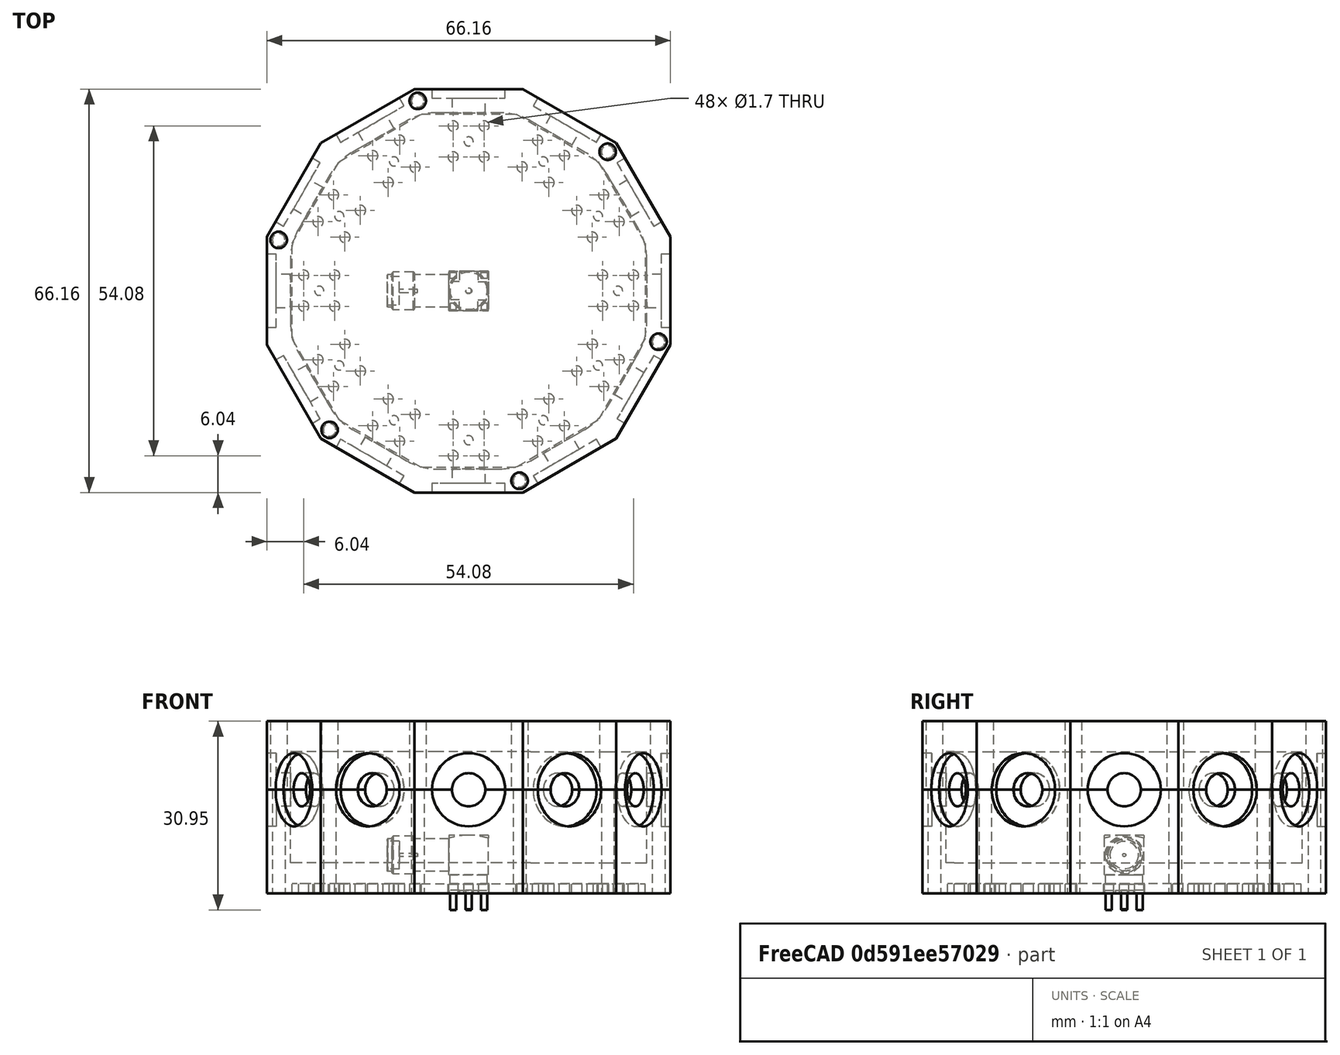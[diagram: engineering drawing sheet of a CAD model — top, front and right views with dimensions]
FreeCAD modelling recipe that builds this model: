
FCSTD DOCUMENT  (FreeCAD 0.19RUnknown)
Label: Case
License: All rights reserved
LicenseURL: http://en.wikipedia.org/wiki/All_rights_reserved
objects: Part::Feature×13, App::Part×13, Sketcher::SketchObject×6, TechDraw::DrawViewPart×6, PartDesign::Pocket×3, PartDesign::PolarPattern×3, PartDesign::Body×3, Part::FeaturePython×3, TechDraw::DrawViewBalloon×3, PartDesign::FeatureBase×2, PartDesign::Hole×2, TechDraw::DrawSVGTemplate×2, TechDraw::DrawViewDimension×2, TechDraw::DrawViewSection×2, TechDraw::DrawPage×2, PartDesign::Pad×1, Spreadsheet::Sheet×1, Part::Part2DObjectPython×1, Part::Extrusion×1, App::DocumentObjectGroup×1
note: 44 computed .brp shape members not serialized (recipe doc carries the construction recipe); baked Part::Feature solids carry a one-line shape summary decoded from their .brp

FEATURE [Sketcher::SketchObject] Sketch  label="Layout"
  FullyConstrained = true
  MapMode = 5
  Support = -> [XY_Plane]
  expr: Constraints[36] = Spreadsheet.outer_diameter
  sketch-geometry (13):
    g0: LineSegment StartX=24.2184 StartY=-24.2184 StartZ=0 EndX=33.083 EndY=-8.86455 EndZ=0
    g1: LineSegment StartX=33.083 StartY=-8.86455 StartZ=0 EndX=33.083 EndY=8.86455 EndZ=0
    g2: LineSegment StartX=33.083 StartY=8.86455 StartZ=0 EndX=24.2184 EndY=24.2184 EndZ=0
    g3: LineSegment StartX=24.2184 StartY=24.2184 StartZ=0 EndX=8.86455 EndY=33.083 EndZ=0
    g4: LineSegment StartX=8.86455 StartY=33.083 StartZ=0 EndX=-8.86455 EndY=33.083 EndZ=0
    g5: LineSegment StartX=-8.86455 StartY=33.083 StartZ=0 EndX=-24.2184 EndY=24.2184 EndZ=0
    g6: LineSegment StartX=-24.2184 StartY=24.2184 StartZ=0 EndX=-33.083 EndY=8.86455 EndZ=0
    g7: LineSegment StartX=-33.083 StartY=8.86455 StartZ=0 EndX=-33.083 EndY=-8.86455 EndZ=0
    g8: LineSegment StartX=-33.083 StartY=-8.86455 StartZ=0 EndX=-24.2184 EndY=-24.2184 EndZ=0
    g9: LineSegment StartX=-24.2184 StartY=-24.2184 StartZ=0 EndX=-8.86455 EndY=-33.083 EndZ=0
    g10: LineSegment StartX=-8.86455 StartY=-33.083 StartZ=0 EndX=8.86455 EndY=-33.083 EndZ=0
    g11: LineSegment StartX=8.86455 StartY=-33.083 StartZ=0 EndX=24.2184 EndY=-24.2184 EndZ=0
    g12: Circle CenterX=0 CenterY=0 CenterZ=0 NormalX=0 NormalY=0 NormalZ=1 AngleXU=0 Radius=34.25
  constraints (28):
    c: Coincident(g0,g1)
    c: Coincident(g1,g2)
    c: Coincident(g2,g3)
    c: Coincident(g3,g4)
    c: Coincident(g4,g5)
    c: Coincident(g5,g6)
    c: Coincident(g6,g7)
    c: Coincident(g7,g8)
    c: Coincident(g8,g9)
    c: Coincident(g9,g10)
    c: Coincident(g10,g11)
    c: Coincident(g11,g0)
    c: Equal(g0, g1-g11) x11
    c: PointOnObject(g0,g12)
    c: PointOnObject(g1,g12)
    c: PointOnObject(g2,g12)
    c: PointOnObject(g3,g12)
    c: PointOnObject(g4,g12)
    c: PointOnObject(g5,g12)
    c: PointOnObject(g6,g12)
    c: PointOnObject(g7,g12)
    c: PointOnObject(g8,g12)
    c: PointOnObject(g9,g12)
    c: PointOnObject(g10,g12)
    c: PointOnObject(g11,g12)
    c: Coincident(g12,g-1)
    c: Diameter(g12) = 68.5
    c: Parallel(g7,g-2)
FEATURE [PartDesign::Pad] Pad  label="Case Body"
  Direction = (1,1,1)
  Length = 28.25
  Length2 = 100
  Profile = -> Sketch
  Refine = true
  Type = 0
  expr: Length = Spreadsheet.casing_total_height
FEATURE [Sketcher::SketchObject] Sketch001  label="Body Cutout"
  AttachmentOffset = pos=(0,0,5) rot=(0,0,1;0rad)
  FullyConstrained = true
  MapMode = 5
  Placement = pos=(0,0,5) rot=(0,0,1;0rad)
  Support = -> [XY_Plane]
  expr: .AttachmentOffset.Base.z = Spreadsheet.casing_bottom_thickness
  expr: Constraints[13] = Spreadsheet.inner_diameter
  expr: Constraints[63] = Spreadsheet.inner_fillet_radius
  expr: Constraints[69] = Spreadsheet.inner_fillet_radius
  expr: Constraints[71] = Spreadsheet.inner_fillet_radius
  expr: Constraints[64] = Spreadsheet.inner_fillet_radius
  expr: Constraints[65] = Spreadsheet.inner_fillet_radius
  expr: Constraints[66] = Spreadsheet.inner_fillet_radius
  expr: Constraints[67] = Spreadsheet.inner_fillet_radius
  expr: Constraints[68] = Spreadsheet.inner_fillet_radius
  expr: Constraints[70] = Spreadsheet.inner_fillet_radius
  expr: Constraints[72] = Spreadsheet.inner_fillet_radius
  expr: Constraints[73] = Spreadsheet.inner_fillet_radius
  expr: Constraints[74] = Spreadsheet.inner_fillet_radius
  sketch-geometry (37):
    g0: LineSegment StartX=29.2193 StartY=-5.14978 StartZ=0 EndX=29.2193 EndY=5.14978 EndZ=0
    g1: LineSegment StartX=27.8795 StartY=10.1498 StartZ=0 EndX=22.7297 EndY=19.0695 EndZ=0
    g2: LineSegment StartX=19.0695 StartY=22.7297 StartZ=0 EndX=10.1498 EndY=27.8795 EndZ=0
    g3: LineSegment StartX=5.14978 StartY=29.2193 StartZ=0 EndX=-5.14978 EndY=29.2193 EndZ=0
    g4: LineSegment StartX=-10.1498 StartY=27.8795 StartZ=0 EndX=-19.0695 EndY=22.7297 EndZ=0
    g5: LineSegment StartX=-22.7297 StartY=19.0695 StartZ=0 EndX=-27.8795 EndY=10.1498 EndZ=0
    g6: LineSegment StartX=-29.2193 StartY=5.14978 StartZ=0 EndX=-29.2193 EndY=-5.14978 EndZ=0
    g7: LineSegment StartX=-27.8795 StartY=-10.1498 StartZ=0 EndX=-22.7297 EndY=-19.0695 EndZ=0
    g8: LineSegment StartX=-19.0695 StartY=-22.7297 StartZ=0 EndX=-10.1498 EndY=-27.8795 EndZ=0
    g9: LineSegment StartX=-5.14978 StartY=-29.2193 StartZ=0 EndX=5.14978 EndY=-29.2193 EndZ=0
    g10: LineSegment StartX=10.1498 StartY=-27.8795 StartZ=0 EndX=19.0695 EndY=-22.7297 EndZ=0
    g11: LineSegment StartX=22.7297 StartY=-19.0695 StartZ=0 EndX=27.8795 EndY=-10.1498 EndZ=0
    g12: Circle CenterX=0 CenterY=0 CenterZ=0 NormalX=0 NormalY=0 NormalZ=1 AngleXU=0 Radius=30.25
    g13: ArcOfCircle CenterX=-19.2193 CenterY=5.14978 CenterZ=0 NormalX=0 NormalY=0 NormalZ=1 AngleXU=0 Radius=10 StartAngle=2.61799 EndAngle=3.14159
    g14: GeomPoint X=-29.2193 Y=7.82928 Z=0
    g15: ArcOfCircle CenterX=-14.0695 CenterY=14.0695 CenterZ=0 NormalX=0 NormalY=0 NormalZ=1 AngleXU=0 Radius=10 StartAngle=2.0944 EndAngle=2.61799
    g16: GeomPoint X=-21.39 Y=21.39 Z=0
    g17: ArcOfCircle CenterX=-5.14978 CenterY=19.2193 CenterZ=0 NormalX=0 NormalY=0 NormalZ=1 AngleXU=0 Radius=10 StartAngle=1.5708 EndAngle=2.0944
    g18: GeomPoint X=-7.82928 Y=29.2193 Z=0
    g19: ArcOfCircle CenterX=5.14978 CenterY=19.2193 CenterZ=0 NormalX=0 NormalY=0 NormalZ=1 AngleXU=0 Radius=10 StartAngle=1.0472 EndAngle=1.5708
    g20: GeomPoint X=7.82928 Y=29.2193 Z=0
    g21: ArcOfCircle CenterX=14.0695 CenterY=14.0695 CenterZ=0 NormalX=0 NormalY=0 NormalZ=1 AngleXU=0 Radius=10 StartAngle=0.523599 EndAngle=1.0472
    g22: GeomPoint X=21.39 Y=21.39 Z=0
    g23: ArcOfCircle CenterX=19.2193 CenterY=5.14978 CenterZ=0 NormalX=0 NormalY=0 NormalZ=1 AngleXU=0 Radius=10 StartAngle=2e-16 EndAngle=0.523599
    g24: GeomPoint X=29.2193 Y=7.82928 Z=0
    g25: ArcOfCircle CenterX=19.2193 CenterY=-5.14978 CenterZ=0 NormalX=0 NormalY=0 NormalZ=1 AngleXU=0 Radius=10 StartAngle=5.75959 EndAngle=6.28319
    g26: GeomPoint X=29.2193 Y=-7.82928 Z=0
    g27: ArcOfCircle CenterX=14.0695 CenterY=-14.0695 CenterZ=0 NormalX=0 NormalY=0 NormalZ=1 AngleXU=0 Radius=10 StartAngle=5.23599 EndAngle=5.75959
    g28: GeomPoint X=21.39 Y=-21.39 Z=0
    g29: ArcOfCircle CenterX=5.14978 CenterY=-19.2193 CenterZ=0 NormalX=0 NormalY=0 NormalZ=1 AngleXU=0 Radius=10 StartAngle=4.71239 EndAngle=5.23599
    g30: GeomPoint X=7.82928 Y=-29.2193 Z=0
    g31: ArcOfCircle CenterX=-5.14978 CenterY=-19.2193 CenterZ=0 NormalX=0 NormalY=0 NormalZ=1 AngleXU=0 Radius=10 StartAngle=4.18879 EndAngle=4.71239
    g32: GeomPoint X=-7.82928 Y=-29.2193 Z=0
    g33: ArcOfCircle CenterX=-14.0695 CenterY=-14.0695 CenterZ=0 NormalX=0 NormalY=0 NormalZ=1 AngleXU=0 Radius=10 StartAngle=3.66519 EndAngle=4.18879
    g34: GeomPoint X=-21.39 Y=-21.39 Z=0
    g35: ArcOfCircle CenterX=-19.2193 CenterY=-5.14978 CenterZ=0 NormalX=0 NormalY=0 NormalZ=1 AngleXU=0 Radius=10 StartAngle=3.14159 EndAngle=3.66519
    g36: GeomPoint X=-29.2193 Y=-7.82928 Z=0
  constraints (86):
    c: PointOnObject(g24,g12)
    c: PointOnObject(g22,g12)
    c: PointOnObject(g20,g12)
    c: PointOnObject(g18,g12)
    c: PointOnObject(g16,g12)
    c: PointOnObject(g14,g12)
    c: PointOnObject(g36,g12)
    c: PointOnObject(g34,g12)
    c: PointOnObject(g32,g12)
    c: PointOnObject(g30,g12)
    c: PointOnObject(g28,g12)
    c: PointOnObject(g26,g12)
    c: Coincident(g12,g-1)
    c: Diameter(g12) = 60.5
    c: Parallel(g6,g-2)
    c: PointOnObject(g14,g6)
    c: PointOnObject(g14,g5)
    c: Tangent(g6,g13) = -1.5708
    c: Tangent(g5,g13) = -1.5708
    c: PointOnObject(g16,g5)
    c: PointOnObject(g16,g4)
    c: Tangent(g5,g15) = -1.5708
    c: Tangent(g4,g15) = -1.5708
    c: PointOnObject(g18,g4)
    c: PointOnObject(g18,g3)
    c: Tangent(g4,g17) = -1.5708
    c: Tangent(g3,g17) = -1.5708
    c: PointOnObject(g20,g3)
    c: PointOnObject(g20,g2)
    c: Tangent(g3,g19) = -1.5708
    c: Tangent(g2,g19) = -1.5708
    c: PointOnObject(g22,g2)
    c: PointOnObject(g22,g1)
    c: Tangent(g2,g21) = -1.5708
    c: Tangent(g1,g21) = -1.5708
    c: PointOnObject(g24,g1)
    c: PointOnObject(g24,g0)
    c: Tangent(g1,g23) = -1.5708
    c: Tangent(g0,g23) = -1.5708
    c: PointOnObject(g26,g0)
    c: PointOnObject(g26,g11)
    c: Tangent(g0,g25) = -1.5708
    c: Tangent(g11,g25) = -1.5708
    c: PointOnObject(g28,g11)
    c: PointOnObject(g28,g10)
    c: Tangent(g11,g27) = -1.5708
    c: Tangent(g10,g27) = -1.5708
    c: PointOnObject(g30,g10)
    c: PointOnObject(g30,g9)
    c: Tangent(g10,g29) = -1.5708
    c: Tangent(g9,g29) = -1.5708
    c: PointOnObject(g32,g9)
    c: PointOnObject(g32,g8)
    c: Tangent(g9,g31) = -1.5708
    c: Tangent(g8,g31) = -1.5708
    c: PointOnObject(g34,g8)
    c: PointOnObject(g34,g7)
    c: Tangent(g8,g33) = -1.5708
    c: Tangent(g7,g33) = -1.5708
    c: PointOnObject(g36,g7)
    c: PointOnObject(g36,g6)
    c: Tangent(g7,g35) = -1.5708
    c: Tangent(g6,g35) = -1.5708
    c: Radius(g19) = 10
    c: Radius(g21) = 10
    c: Radius(g23) = 10
    c: Radius(g25) = 10
    c: Radius(g27) = 10
    c: Radius(g29) = 10
    c: Radius(g31) = 10
    c: Radius(g33) = 10
    c: Radius(g35) = 10
    c: Radius(g13) = 10
    c: Radius(g15) = 10
    c: Radius(g17) = 10
    c: Horizontal(g3)
    c: Equal(g4,g3)
    c: Equal(g3,g5)
    c: Equal(g5,g6)
    c: Equal(g6,g7)
    c: Equal(g7,g8)
    c: Equal(g8,g9)
    c: Equal(g9,g10)
    c: Equal(g10,g11)
    c: Equal(g11,g0)
    c: Equal(g0,g1)
FEATURE [PartDesign::Pocket] Pocket  label="Body Pocket"
  BaseFeature = -> Pad
  Length = 18.25
  Length2 = 100
  Profile = -> Sketch001
  Refine = true
  Reversed = true
  Type = 0
  expr: Length = Spreadsheet.casing_pocket_height
FEATURE [Part::Feature] Part__Feature  label="SOLID"
  shape: bbox 17.95 x 11.53 x 14.41 mm, 73 faces (baked)
FEATURE [Part::Feature] Part__Feature008  label="SOLID008"
  shape: bbox 17.95 x 11.53 x 14.41 mm, 73 faces (baked)
FEATURE [App::Part] HJ_SMA003008  label="HJ-SMA011"
  Group = -> [Part__Feature008]
  Origin = -> Origin008
  Placement = pos=(-12.25,21.2176,1.65) rot=(0,0,-1;1.0472rad)
FEATURE [Part::Feature] Part__Feature005  label="SOLID005"
  shape: bbox 17.95 x 11.53 x 14.41 mm, 73 faces (baked)
FEATURE [App::Part] HJ_SMA003005  label="HJ-SMA008"
  Group = -> [Part__Feature005]
  Origin = -> Origin005
  Placement = pos=(-21.2176,-12.25,1.65) rot=(0,0,1;0.523599rad)
FEATURE [Part::Feature] Part__Feature002  label="SOLID002"
  shape: bbox 17.95 x 11.53 x 14.41 mm, 73 faces (baked)
FEATURE [App::Part] HJ_SMA003002  label="HJ-SMA005"
  Group = -> [Part__Feature002]
  Origin = -> Origin002
  Placement = pos=(12.25,-21.2176,1.65) rot=(0,0,1;2.0944rad)
FEATURE [Part::Feature] Part__Feature001  label="SOLID001"
  shape: bbox 17.95 x 11.53 x 14.41 mm, 73 faces (baked)
FEATURE [App::Part] HJ_SMA003001  label="HJ-SMA004"
  Group = -> [Part__Feature001]
  Origin = -> Origin001
  Placement = pos=(21.2176,-12.25,1.65) rot=(0,0,1;2.61799rad)
FEATURE [Part::Feature] Part__Feature009  label="SOLID009"
  shape: bbox 17.95 x 11.53 x 14.41 mm, 73 faces (baked)
FEATURE [Part::Feature] Part__Feature007  label="SOLID007"
  shape: bbox 17.95 x 11.53 x 14.41 mm, 73 faces (baked)
FEATURE [App::Part] HJ_SMA003  label="HJ-SMA003"
  Group = -> [Part__Feature]
  Origin = -> Origin009
  Placement = pos=(24.5,0,1.65) rot=(0,0,1;3.14159rad)
FEATURE [Part::Feature] Part__Feature003  label="SOLID003"
  shape: bbox 17.95 x 11.53 x 14.41 mm, 73 faces (baked)
FEATURE [Part::Feature] Part__Feature010  label="SOLID010"
  shape: bbox 17.95 x 11.53 x 14.41 mm, 73 faces (baked)
FEATURE [App::Part] HJ_SMA003010  label="HJ-SMA013"
  Group = -> [Part__Feature010]
  Origin = -> Origin010
  Placement = pos=(12.25,21.2176,1.65) rot=(0,0,1;4.18879rad)
FEATURE [App::Part] HJ_SMA003007  label="HJ-SMA010"
  Group = -> [Part__Feature007]
  Origin = -> Origin007
  Placement = pos=(-21.2176,12.25,1.65) rot=(0,0,-1;0.523599rad)
FEATURE [App::Part] HJ_SMA003003  label="HJ-SMA006"
  Group = -> [Part__Feature003]
  Origin = -> Origin003
  Placement = pos=(0,-24.5,1.65) rot=(0,0,1;1.5708rad)
FEATURE [Part::Feature] Part__Feature006  label="SOLID006"
  shape: bbox 17.95 x 11.53 x 14.41 mm, 73 faces (baked)
FEATURE [App::Part] HJ_SMA003006  label="HJ-SMA009"
  Group = -> [Part__Feature006]
  Origin = -> Origin006
  Placement = pos=(-24.5,0,1.65) rot=(0,0,1;0rad)
FEATURE [App::Part] HJ_SMA003009  label="HJ-SMA012"
  Group = -> [Part__Feature009]
  Origin = -> Origin012
  Placement = pos=(0,24.5,1.65) rot=(0,0,-1;1.5708rad)
FEATURE [Part::Feature] Part__Feature011  label="SOLID011"
  shape: bbox 17.95 x 11.53 x 14.41 mm, 73 faces (baked)
FEATURE [Part::Feature] Part__Feature012  label="resistive-power-splitter PCB"
  shape: bbox 57.96 x 57.96 x 1.6 mm, 74 faces (baked)
FEATURE [App::Part] HJ_SMA003011  label="HJ-SMA014"
  Group = -> [Part__Feature011]
  Origin = -> Origin011
  Placement = pos=(21.2176,12.25,1.65) rot=(0,0,1;3.66519rad)
FEATURE [Part::Feature] Part__Feature004  label="SOLID004"
  shape: bbox 17.95 x 11.53 x 14.41 mm, 73 faces (baked)
FEATURE [App::Part] HJ_SMA003004  label="HJ-SMA007"
  Group = -> [Part__Feature004]
  Origin = -> Origin004
  Placement = pos=(-12.25,-21.2176,1.65) rot=(0,0,1;1.0472rad)
FEATURE [App::Part] resistive_power_splitter_1  label="resistive-power-splitter"
  Group = -> [HJ_SMA003,HJ_SMA003001,HJ_SMA003002,HJ_SMA003003,HJ_SMA003004,HJ_SMA003005,HJ_SMA003006,HJ_SMA003007,HJ_SMA003008,HJ_SMA003009,HJ_SMA003010,HJ_SMA003011,Part__Feature012]
  Origin = -> Origin013
  Placement = pos=(0,0,9.1) rot=(0,0,1;0rad)
  expr: .Placement.Base.z = Spreadsheet.pcb_height
FEATURE [Spreadsheet::Sheet] Spreadsheet
  cells = A1=Outer Diameter; B1(outer_diameter)==B2 + 2 * B3; A2=Inner Diameter; B2(inner_diameter)==60.5mm; A3=Input: Wall Thickness; B3(wall_thickness)==4mm; A4=Screw Diameter; B4(screw_diameter)==2.5mm; A5=Inner Fillet Radius; B5(inner_fillet_radius)==10mm; A6=SMA Hole Diameter; B6(sma_hole_diameter)==E6 + G6; C6=Diameter specified by HJ-Tech is 5.35 mm ± 0.1 mm; probably needs some tolerance; D6=SMA Hole Diameter; E6==5.35mm; F6=SMA Hole Tolerance; G6==0.1mm; A7=SMA Pocket Diameter; B7(sma_pocket_diameter)==12mm; A8=SMA Pocket Depth; B8(sma_pocket_depth)==B3 - B23; A9=SMA Hole Height; B9(sma_hole_height)==B15 + B14 + B12 + B11; C9=This is also the case bottom height.; A10=SMA Connector Total Height; B10==12.25mm; A11=SMA Connector Hole Height; B11==6.3mm; C11=Height above top of PCB; A12=SMA Connector Bottom Height; B12==2.7mm; C12=Height from top of PCB to bottom of connector; A13=SMA Connector Top Height; B13==B10 - B12; C13=Height from top of PCB to top of connector; A14=Input: Vertical Gap; B14==3mm; C14=Vertical gap inside casing from top/bottom of PCBA to casing; A15=Casing Bottom Thickness; B15(casing_bottom_thickness)==5mm; A16=Casing Top Thickness; B16(casing_top_thickness)==5mm; A17=Casing Total Height; B17(casing_total_height)==B15 + B16 + 2 * B14 + B10; A18=Casing Pocket Height; B18(casing_pocket_height)==B17 - (B15 + B16); A19=PCB Thickness; B19==1.6mm; A20=PCB Height; B20(pcb_height)==B15 + B14 + B12 - B19; C20=Height of bottom of PCB; A21=Casing Top Height; B21(casing_top_height)==B17 - B9; A22=Casing Bottom Screw Depth; B22(casing_bottom_screw_depth)==B9; A23=SMA Connector Wall Depth; B23==2.5mm; C23=Keeping this fixed and calculating SMA pocket depth from this so that connectors still fit if wall thickness is changed.
FEATURE [Sketcher::SketchObject] Sketch002  label="SMA Connector Hole Sketch"
  FullyConstrained = true
  MapMode = 5
  Placement = pos=(4.906e-13,-33.083,0) rot=(1,0,0;1.5708rad)
  Support = -> [Pocket]
  expr: Constraints[2] = Spreadsheet.sma_hole_height
  expr: Constraints[1] = Spreadsheet.sma_hole_diameter
  sketch-geometry (1):
    g0: Circle CenterX=0 CenterY=17 CenterZ=0 NormalX=0 NormalY=0 NormalZ=1 AngleXU=0 Radius=2.725
  constraints (3):
    c: PointOnObject(g0,g-2)
    c: Diameter(g0) = 5.45
    c: DistanceY(g-1,g0) = 17
FEATURE [PartDesign::Pocket] Pocket001  label="SMA Connector Hole Pocket"
  BaseFeature = -> Pocket
  Length = 4
  Length2 = 100
  Profile = -> Sketch002
  Refine = true
  Type = 0
  expr: Length = Spreadsheet.wall_thickness
FEATURE [Sketcher::SketchObject] Sketch003  label="SMA Connector Pocket Sketch"
  ExternalGeometry = -> [Pocket001]
  FullyConstrained = true
  MapMode = 5
  Placement = pos=(4.906e-13,-33.083,0) rot=(1,0,0;1.5708rad)
  Support = -> [Pocket001]
  expr: Constraints[1] = Spreadsheet.sma_pocket_diameter
  sketch-geometry (1):
    g0: Circle CenterX=0 CenterY=17 CenterZ=0 NormalX=0 NormalY=0 NormalZ=1 AngleXU=0 Radius=6
  constraints (2):
    c: Coincident(g0,g-3)
    c: Diameter(g0) = 12
FEATURE [PartDesign::Pocket] Pocket002  label="SMA Connector Pocket"
  BaseFeature = -> Pocket001
  Length = 1.5
  Length2 = 100
  Profile = -> Sketch003
  Refine = true
  Type = 0
  expr: Length = Spreadsheet.sma_pocket_depth
FEATURE [PartDesign::PolarPattern] PolarPattern
  Angle = 360
  Axis = -> Z_Axis
  BaseFeature = -> Pocket002
  Occurrences = 12
  Originals = -> [Pocket002,Pocket001]
  Refine = true
FEATURE [PartDesign::Body] Body  label="Case Full"
  Group = -> [Sketch,Pad,Sketch001,Pocket,Sketch002,Pocket001,Sketch003,Pocket002,PolarPattern]
  Origin = -> Origin
  Tip = -> PolarPattern
FEATURE [Part::Part2DObjectPython] Line  # Draft 2D object (typed FeaturePython)
  Area = 0
  ChamferSize = 0
  Closed = false
  End = (-50,50,17)
  FilletRadius = 0
  Length = 100
  MakeFace = false
  Placement = pos=(-97.8345,10.59,0) rot=(0,0,1;0rad)
  Points = (2) [(47.8345,-60.59,17),(47.8345,39.41,17)]
  Start = (-50,-50,17)
  Subdivisions = 0
  expr: .End.z = Spreadsheet.sma_hole_height
  expr: .Start.z = Spreadsheet.sma_hole_height
FEATURE [Part::Extrusion] Extrude
  Base = -> Line
  Dir = (1,0,0)
  DirMode = 0
  FaceMakerClass = Part::FaceMakerBullseye
  LengthFwd = 100
  LengthRev = 0
  Solid = false
  Symmetric = false
FEATURE [Part::FeaturePython] Slice  # WARN: FeaturePython — macro-defined, semantics opaque (R4)
  Base = -> PolarPattern
  Mode = 1
  Tolerance = 0
  Tools = -> [Extrude]
FEATURE [Part::FeaturePython] Slice_child0  label="Case Bottom"  # WARN: FeaturePython — macro-defined, semantics opaque (R4)
  Base = -> Slice
  FilterType = 1
  Invert = false
  OverrideMaxVal = 0
  WindowFrom = 80
  WindowTo = 100
  items = 0
FEATURE [Part::FeaturePython] Slice_child1  label="Case Top"  # WARN: FeaturePython — macro-defined, semantics opaque (R4)
  Base = -> Slice
  FilterType = 1
  Invert = false
  OverrideMaxVal = 0
  WindowFrom = 80
  WindowTo = 100
  items = 1
FEATURE [App::DocumentObjectGroup] GrExplode_Slice  label="Exploded Slice"
  Group = -> [Slice_child0,Slice_child1]
FEATURE [PartDesign::FeatureBase] BaseFeature
  BaseFeature = -> Slice_child0
FEATURE [PartDesign::FeatureBase] BaseFeature001
  BaseFeature = -> Slice_child1
FEATURE [Sketcher::SketchObject] Sketch004  label="Bottom Screw Hole"
  FullyConstrained = true
  MapMode = 5
  Placement = pos=(0,0,17) rot=(0,0,1;0rad)
  Support = -> [BaseFeature]
  expr: Constraints[6] = Spreadsheet.screw_diameter
  expr: Constraints[1] = (Spreadsheet.inner_diameter + Spreadsheet.outer_diameter) / 2
  sketch-geometry (3):
    g0: Circle CenterX=0 CenterY=0 CenterZ=0 NormalX=0 NormalY=0 NormalZ=1 AngleXU=0 Radius=32.25
    g1: LineSegment StartX=0 StartY=0 StartZ=0 EndX=-12.941 EndY=48.2963 EndZ=0
    g2: Circle CenterX=-8.34691 CenterY=31.1511 CenterZ=0 NormalX=0 NormalY=0 NormalZ=1 AngleXU=0 Radius=1.25
  constraints (8):
    c: Coincident(g0,g-1)
    c: Diameter(g0) = 64.5
    c: Coincident(g1,g-1)
    c: Distance(g1) = 50
    c: Angle(g-2,g1) = 0.261799
    c: PointOnObject(g2,g0)
    c: Diameter(g2) = 2.5
    c: PointOnObject(g2,g1)
FEATURE [PartDesign::Hole] Hole  label="Threaded Screw Hole"
  BaseFeature = -> BaseFeature
  Depth = 17
  DepthType = 0
  Diameter = 2.05
  DrillForDepth = false
  DrillPoint = 1
  DrillPointAngle = 118
  HoleCutCountersinkAngle = 90
  HoleCutCustomValues = false
  HoleCutDepth = 0
  HoleCutDiameter = 6.1
  HoleCutType = 0
  ModelActualThread = false
  Profile = -> Sketch004
  Refine = true
  Tapered = false
  TaperedAngle = 90
  ThreadAngle = 60
  ThreadClass = 0
  ThreadCutOffInner = 0.0487139
  ThreadCutOffOuter = 0.0974279
  ThreadDirection = 0
  ThreadFit = 0
  ThreadPitch = 0.45
  ThreadSize = 8
  ThreadType = 1
  Threaded = true
  expr: Depth = Spreadsheet.casing_bottom_screw_depth
FEATURE [PartDesign::PolarPattern] PolarPattern001  label="Repeated Screw Holes"
  Angle = 360
  Axis = -> Sketch004 [N_Axis]
  BaseFeature = -> Hole
  Occurrences = 6
  Originals = -> [Hole]
  Refine = true
FEATURE [PartDesign::Body] Body001  label="Case Bottom Body"
  BaseFeature = -> Slice_child0
  Group = -> [BaseFeature,Sketch004,Hole,PolarPattern001]
  Origin = -> Origin014
  Tip = -> PolarPattern001
FEATURE [Sketcher::SketchObject] Sketch005  label="Top Screw Hole"
  FullyConstrained = true
  MapMode = 5
  Placement = pos=(0,0,28.25) rot=(0,0,1;0rad)
  Support = -> [BaseFeature001]
  expr: Constraints[7] = Spreadsheet.screw_diameter
  expr: Constraints[1] = (Spreadsheet.inner_diameter + Spreadsheet.outer_diameter) / 2
  sketch-geometry (3):
    g0: Circle CenterX=0 CenterY=0 CenterZ=0 NormalX=0 NormalY=0 NormalZ=1 AngleXU=0 Radius=32.25
    g1: LineSegment StartX=0 StartY=0 StartZ=0 EndX=-12.941 EndY=48.2963 EndZ=0
    g2: Circle CenterX=-8.34691 CenterY=31.1511 CenterZ=0 NormalX=0 NormalY=0 NormalZ=1 AngleXU=0 Radius=1.25
  constraints (8):
    c: Coincident(g0,g-1)
    c: Diameter(g0) = 64.5
    c: Coincident(g1,g-1)
    c: Distance(g1) = 50
    c: Angle(g-2,g1) = 0.261799
    c: PointOnObject(g2,g1)
    c: PointOnObject(g2,g0)
    c: Diameter(g2) = 2.5
FEATURE [PartDesign::Hole] Hole001  label="Screw Hole"
  BaseFeature = -> BaseFeature001
  Depth = 11.25
  DepthType = 0
  Diameter = 2.7
  DrillForDepth = false
  DrillPoint = 1
  DrillPointAngle = 118
  HoleCutCountersinkAngle = 90
  HoleCutCustomValues = false
  HoleCutDepth = 0
  HoleCutDiameter = 6.1
  HoleCutType = 0
  ModelActualThread = false
  Profile = -> Sketch005
  Refine = true
  Tapered = false
  TaperedAngle = 90
  ThreadAngle = 0
  ThreadClass = 0
  ThreadCutOffInner = 0
  ThreadCutOffOuter = 0
  ThreadDirection = 0
  ThreadFit = 1
  ThreadPitch = 0
  ThreadSize = 8
  ThreadType = 1
  Threaded = false
  expr: Depth = Spreadsheet.casing_top_height
FEATURE [PartDesign::PolarPattern] PolarPattern002  label="Repeated Top Screw Holes"
  Angle = 360
  Axis = -> Sketch005 [N_Axis]
  BaseFeature = -> Hole001
  Occurrences = 6
  Originals = -> [Hole001]
  Refine = true
FEATURE [PartDesign::Body] Body002  label="Case Top Body"
  BaseFeature = -> Slice_child1
  Group = -> [BaseFeature001,Sketch005,Hole001,PolarPattern002]
  Origin = -> Origin015
  Tip = -> PolarPattern002
FEATURE [TechDraw::DrawSVGTemplate] Template
  EditableTexts = AUTHOR_NAME=Andreas Müller; DRAWING_TITLE=Gehäuse Oberteil; FC-DATE=11.3.2022; FC-REV=REV A; FC-SH=1 / 1; FC-SI=A4
  Height = 210
  Orientation = 1
  Width = 297
FEATURE [TechDraw::DrawSVGTemplate] Template001
  EditableTexts = AUTHOR_NAME=Andreas Müller; DRAWING_TITLE=Gehäuse Unterteil; FC-DATE=11.3.2022; FC-REV=REV A; FC-SH=1 / 1; FC-SI=A4
  Height = 210
  Orientation = 1
  Width = 297
FEATURE [TechDraw::DrawViewPart] View  label="Isometric View"
  CoarseView = false
  Direction = (0.577,-0.577,0.577)
  Focus = 100
  HardHidden = false
  IsoCount = 0
  IsoHidden = false
  IsoVisible = false
  LockPosition = false
  Perspective = false
  Rotation = 0
  ScaleType = 0
  SeamHidden = false
  SeamVisible = true
  SmoothHidden = false
  SmoothVisible = true
  Source = -> [Body002]
  X = 61.3904
  XDirection = (0.707,0.707,0)
  Y = 113.412
FEATURE [TechDraw::DrawViewBalloon] Balloon
  BubbleShape = 3
  EndType = 0
  EndTypeScale = 1
  KinkLength = 5
  LockPosition = false
  OriginX = -16.3629
  OriginY = 20.2401
  Rotation = 0
  ScaleType = 0
  ShapeScale = 1
  SourceView = -> View
  Text = 6x M2.5 Loch
  TextWrapLen = -1
  X = 3.50972
  Y = 40.2401
FEATURE [TechDraw::DrawViewPart] View002  label="Top View"
  CoarseView = false
  Direction = (0,0,1)
  Focus = 100
  HardHidden = false
  IsoCount = 0
  IsoHidden = false
  IsoVisible = false
  LockPosition = false
  Perspective = false
  Rotation = 0
  ScaleType = 0
  SeamHidden = false
  SeamVisible = true
  SmoothHidden = false
  SmoothVisible = true
  Source = -> [Body002]
  X = 150.826
  XDirection = (1,0,0)
  Y = 115.416
FEATURE [TechDraw::DrawViewDimension] Dimension003
  Arbitrary = false
  ArbitraryTolerances = false
  EqualTolerance = true
  FormatSpec = ⌀%.2f
  FormatSpecOverTolerance = %+.2f
  FormatSpecUnderTolerance = %+.2f
  Inverted = false
  LockPosition = false
  MeasureType = 1
  OverTolerance = 0
  References2D = -> [View002]
  Rotation = 0
  ScaleType = 0
  TheoreticalExact = false
  Type = 5
  UnderTolerance = 0
  X = 3.48762
  Y = 25.2504
FEATURE [TechDraw::DrawViewPart] View003  label="Side View"
  CoarseView = false
  Direction = (0,-1,0)
  Focus = 100
  HardHidden = false
  IsoCount = 0
  IsoHidden = false
  IsoVisible = false
  LockPosition = false
  Perspective = false
  Rotation = 0
  ScaleType = 0
  SeamHidden = false
  SeamVisible = true
  SmoothHidden = false
  SmoothVisible = true
  Source = -> [Body002]
  X = 235.044
  XDirection = (1,0,0)
  Y = 129.524
FEATURE [TechDraw::DrawViewPart] View004  label="Isometric View001"
  CoarseView = false
  Direction = (0.577,-0.577,0.577)
  Focus = 100
  HardHidden = false
  IsoCount = 0
  IsoHidden = false
  IsoVisible = false
  LockPosition = false
  Perspective = false
  Rotation = 0
  ScaleType = 0
  SeamHidden = false
  SeamVisible = true
  SmoothHidden = false
  SmoothVisible = true
  Source = -> [Body001]
  X = 63.634
  XDirection = (0.707,0.707,0)
  Y = 112.733
FEATURE [TechDraw::DrawViewPart] View005  label="Top View001"
  CoarseView = false
  Direction = (0,0,1)
  Focus = 100
  HardHidden = false
  IsoCount = 0
  IsoHidden = false
  IsoVisible = false
  LockPosition = false
  Perspective = false
  Rotation = 0
  ScaleType = 0
  SeamHidden = false
  SeamVisible = true
  SmoothHidden = false
  SmoothVisible = true
  Source = -> [Body001]
  X = 149.345
  XDirection = (1,0,0)
  Y = 113.862
FEATURE [TechDraw::DrawViewPart] View006  label="Side View001"
  CoarseView = false
  Direction = (0,-1,0)
  Focus = 100
  HardHidden = false
  IsoCount = 0
  IsoHidden = false
  IsoVisible = false
  LockPosition = false
  Perspective = false
  Rotation = 0
  ScaleType = 0
  SeamHidden = false
  SeamVisible = true
  SmoothHidden = false
  SmoothVisible = true
  Source = -> [Body001]
  X = 239.173
  XDirection = (1,0,0)
  Y = 131.616
FEATURE [TechDraw::DrawViewBalloon] Balloon001
  BubbleShape = 3
  EndType = 0
  EndTypeScale = 1
  KinkLength = 5
  LockPosition = false
  OriginX = -16.5164
  OriginY = 23.3445
  Rotation = 0
  ScaleType = 0
  ShapeScale = 1
  SourceView = -> View004
  Text = 6x M2.5 Gewinde
  TextWrapLen = -1
  X = 3.48355
  Y = 43.3445
FEATURE [TechDraw::DrawViewSection] SectionView  label="Section  - "
  BaseView = -> View003
  CoarseView = false
  CutSurfaceDisplay = 2
  Direction = (1,0,0)
  FileGeomPattern = <path>
  FileHatchPattern = <path>
  Focus = 100
  FuseBeforeCut = false
  HardHidden = false
  HatchScale = 1
  IsoCount = 0
  IsoHidden = false
  IsoVisible = false
  LockPosition = false
  NameGeomPattern = Diamond
  Perspective = false
  Rotation = 0
  ScaleType = 0
  SeamHidden = false
  SeamVisible = true
  SectionDirection = 1
  SectionNormal = (1,0,0)
  SectionOrigin = (9,0,22.62)
  SmoothHidden = false
  SmoothVisible = true
  Source = -> [Body002]
  X = 235.586
  XDirection = (0,1,0)
  Y = 98.0594
FEATURE [TechDraw::DrawPage] Page  label="Case Top Drawing"
  KeepUpdated = true
  NextBalloonIndex = 3
  ProjectionType = 0
  Template = -> Template
  Views = -> [View,Balloon,View002,Dimension003,View003,SectionView]
FEATURE [TechDraw::DrawViewSection] SectionView001  label="Section  - 001"
  BaseView = -> View006
  CoarseView = false
  CutSurfaceDisplay = 2
  Direction = (1,0,0)
  FileGeomPattern = <path>
  FileHatchPattern = <path>
  Focus = 100
  FuseBeforeCut = false
  HardHidden = false
  HatchScale = 1
  IsoCount = 0
  IsoHidden = false
  IsoVisible = false
  LockPosition = false
  NameGeomPattern = Diamond
  Perspective = false
  Rotation = 0
  ScaleType = 0
  SeamHidden = false
  SeamVisible = true
  SectionDirection = 1
  SectionNormal = (1,0,0)
  SectionOrigin = (9,0,8.5)
  SmoothHidden = false
  SmoothVisible = true
  Source = -> [Body001]
  X = 238.664
  XDirection = (0,1,0)
  Y = 95.1941
FEATURE [TechDraw::DrawViewBalloon] Balloon002
  BubbleShape = 3
  EndType = 0
  EndTypeScale = 1
  KinkLength = 5
  LockPosition = false
  OriginX = -31.3232
  OriginY = -7.81184
  Rotation = 0
  ScaleType = 0
  ShapeScale = 1
  SourceView = -> SectionView001
  Text = Loch & Gewinde nicht zwingend durchgehend
  TextWrapLen = -1
  X = -7.83555
  Y = -30.0575
FEATURE [TechDraw::DrawViewDimension] Dimension
  Arbitrary = false
  ArbitraryTolerances = false
  EqualTolerance = true
  FormatSpec = %.2f
  FormatSpecOverTolerance = %+.2f
  FormatSpecUnderTolerance = %+.2f
  Inverted = false
  LockPosition = false
  MeasureType = 1
  OverTolerance = 0
  References2D = -> [SectionView001]
  Rotation = 0
  ScaleType = 0
  TheoreticalExact = false
  Type = 2
  UnderTolerance = 0
  X = -41.9711
  Y = 2.93414
FEATURE [TechDraw::DrawPage] Page001  label="Case Bottom Drawing"
  KeepUpdated = true
  NextBalloonIndex = 3
  ProjectionType = 0
  Template = -> Template001
  Views = -> [View004,View005,View006,Balloon001,SectionView001,Balloon002,Dimension]
note: 4 file-system paths scrubbed to <path> (originals preserved in the JSON sidecar)
